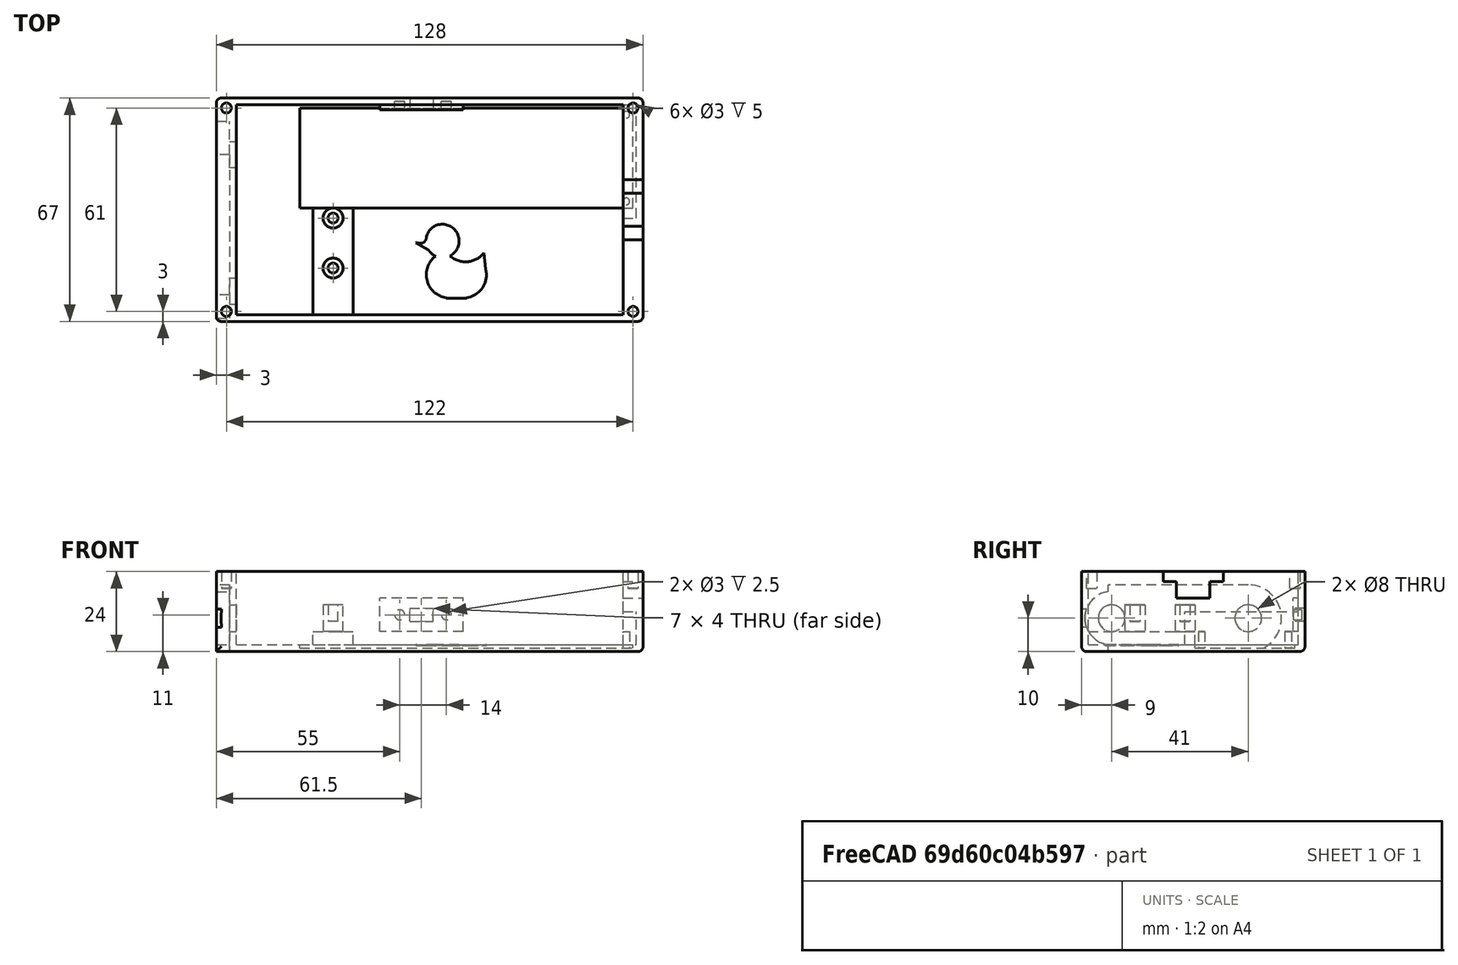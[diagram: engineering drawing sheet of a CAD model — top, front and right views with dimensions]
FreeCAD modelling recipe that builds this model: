
FCSTD DOCUMENT  (FreeCAD 1.0R39319 (Git))
Label: caseBottomV2
License: All rights reserved
LicenseURL: https://en.wikipedia.org/wiki/All_rights_reserved
objects: PartDesign::SubtractiveCylinder×16, PartDesign::SubtractiveBox×9, PartDesign::AdditiveCylinder×6, PartDesign::AdditiveBox×3, PartDesign::Fillet×1, PartDesign::SubtractivePrism×1, PartDesign::Body×1
note: 109 computed .brp shape members not serialized (recipe doc carries the construction recipe); baked Part::Feature solids carry a one-line shape summary decoded from their .brp

FEATURE [PartDesign::AdditiveBox] Box  label="base"
  AttacherType = Attacher::AttachEngine3D
  Height = 24
  Length = 128
  Refine = true
  Suppressed = false
  Width = 67
FEATURE [PartDesign::SubtractiveBox] Box001  label="primaryHollow"
  AttacherType = Attacher::AttachEngine3D
  AttachmentOffset = pos=(6,2,-22) rot=(0,0,1;0rad)
  AttachmentSupport = -> [Box]
  BaseFeature = -> Box
  Height = 22
  Length = 116
  MapMode = 5
  Placement = pos=(6,2,2) rot=(0,0,1;0rad)
  Refine = true
  Suppressed = false
  Width = 63
FEATURE [PartDesign::SubtractiveBox] Box002  label="batteryPCBRearNotch"
  AttacherType = Attacher::AttachEngine3D
  AttachmentOffset = pos=(116,29,0) rot=(0,0,1;0rad)
  AttachmentSupport = -> [Box001]
  BaseFeature = -> Box001
  Height = 10
  Length = 4
  MapMode = 5
  Placement = pos=(122,31,2) rot=(0,0,1;0rad)
  Refine = true
  Suppressed = false
  Width = 34
FEATURE [PartDesign::SubtractiveBox] Box003  label="batteryPCBRecess"
  AttacherType = Attacher::AttachEngine3D
  AttachmentOffset = pos=(-97,3,-1) rot=(0,0,1;0rad)
  AttachmentSupport = -> [Box002]
  BaseFeature = -> Box002
  Height = 1
  Length = 100
  MapMode = 5
  Placement = pos=(25,34,1) rot=(0,0,1;0rad)
  Refine = true
  Suppressed = false
  Width = 30
FEATURE [PartDesign::AdditiveBox] Box004  label="DACRearStand"
  AttacherType = Attacher::AttachEngine3D
  AttachmentOffset = pos=(4,-32,1) rot=(0,0,1;0rad)
  AttachmentSupport = -> [Box003]
  BaseFeature = -> Box003
  Height = 4
  Length = 12
  MapMode = 2
  Placement = pos=(29,2,2) rot=(0,0,1;0rad)
  Refine = true
  Suppressed = false
  Width = 32
FEATURE [PartDesign::AdditiveCylinder] Cylinder  label="DACLeftScrewSupport"
  Angle = 360
  AttacherType = Attacher::AttachEngine3D
  AttachmentOffset = pos=(6,14,0) rot=(0,0,1;0rad)
  AttachmentSupport = -> [Box004]
  BaseFeature = -> Box004
  FirstAngle = 0
  Height = 8
  MapMode = 5
  Placement = pos=(35,16,6) rot=(0,0,1;0rad)
  Radius = 3
  Refine = true
  SecondAngle = 0
  Suppressed = false
FEATURE [PartDesign::AdditiveCylinder] Cylinder001  label="DACRightScrewSupport"
  Angle = 360
  AttacherType = Attacher::AttachEngine3D
  AttachmentOffset = pos=(0,15,0) rot=(0,0,1;0rad)
  AttachmentSupport = -> [Cylinder]
  BaseFeature = -> Cylinder
  FirstAngle = 0
  Height = 8
  MapMode = 5
  Placement = pos=(35,31,6) rot=(0,0,1;0rad)
  Radius = 3
  Refine = true
  SecondAngle = 0
  Suppressed = false
FEATURE [PartDesign::SubtractiveCylinder] Cylinder002  label="DACRightScrewHollow"
  Angle = 360
  AttacherType = Attacher::AttachEngine3D
  AttachmentOffset = pos=(0,0,-5) rot=(0,0,1;0rad)
  AttachmentSupport = -> [Cylinder001]
  BaseFeature = -> Cylinder001
  FirstAngle = 0
  Height = 5
  MapMode = 5
  Placement = pos=(35,31,9) rot=(0,0,1;0rad)
  Radius = 1.5
  Refine = true
  SecondAngle = 0
  Suppressed = false
FEATURE [PartDesign::SubtractiveCylinder] Cylinder003  label="DACLeftScrewHollow"
  Angle = 360
  AttacherType = Attacher::AttachEngine3D
  AttachmentOffset = pos=(0,-15,-5) rot=(0,0,1;0rad)
  AttachmentSupport = -> [Cylinder002]
  BaseFeature = -> Cylinder002
  FirstAngle = 0
  Height = 5
  MapMode = 5
  Placement = pos=(35,16,9) rot=(0,0,1;0rad)
  Radius = 1.5
  Refine = true
  SecondAngle = 0
  Suppressed = false
FEATURE [PartDesign::SubtractiveBox] Box005  label="DACInset"
  AttacherType = Attacher::AttachEngine3D
  AttachmentOffset = pos=(-34,-9,-4) rot=(0,0,1;0rad)
  AttachmentSupport = -> [Cylinder003]
  BaseFeature = -> Cylinder003
  Height = 4
  Length = 42
  MapMode = 5
  Placement = pos=(4,50,0) rot=(0.57735,-0.57735,-0.57735;2.0944rad)
  Refine = true
  Suppressed = false
  Width = 20
FEATURE [PartDesign::SubtractiveCylinder] Cylinder004  label="volumeKnobHole"
  Angle = 360
  AttacherType = Attacher::AttachEngine3D
  AttachmentOffset = pos=(0,10,-6) rot=(0,0,1;0rad)
  AttachmentSupport = -> [Box005]
  BaseFeature = -> Box005
  FirstAngle = 0
  Height = 6
  MapMode = 5
  Placement = pos=(6,50,10) rot=(0.57735,-0.57735,-0.57735;2.0944rad)
  Radius = 4
  Refine = true
  SecondAngle = 0
  Suppressed = false
FEATURE [PartDesign::SubtractiveCylinder] Cylinder005  label="headphoneJackHole"
  Angle = 360
  AttacherType = Attacher::AttachEngine3D
  AttachmentOffset = pos=(41,0,-6) rot=(0,0,1;0rad)
  AttachmentSupport = -> [Cylinder004]
  BaseFeature = -> Cylinder004
  FirstAngle = 0
  Height = 6
  MapMode = 5
  Placement = pos=(6,9,10) rot=(0.57735,-0.57735,-0.57735;2.0944rad)
  Radius = 4
  Refine = true
  SecondAngle = 0
  Suppressed = false
FEATURE [PartDesign::SubtractiveCylinder] Cylinder006  label="volumeKnobRecess"
  Angle = 360
  AttacherType = Attacher::AttachEngine3D
  AttachmentOffset = pos=(-41,0,-4) rot=(0,0,1;0rad)
  AttachmentSupport = -> [Cylinder005]
  BaseFeature = -> Cylinder005
  FirstAngle = 0
  Height = 4
  MapMode = 5
  Placement = pos=(4,50,10) rot=(0.57735,-0.57735,-0.57735;2.0944rad)
  Radius = 10
  Refine = true
  SecondAngle = 0
  Suppressed = false
FEATURE [PartDesign::SubtractiveCylinder] Cylinder007  label="headphoneJackRecess"
  Angle = 360
  AttacherType = Attacher::AttachEngine3D
  AttachmentOffset = pos=(41,0,-4) rot=(0,0,1;0rad)
  AttachmentSupport = -> [Cylinder006]
  BaseFeature = -> Cylinder006
  FirstAngle = 0
  Height = 4
  MapMode = 5
  Placement = pos=(4,9,10) rot=(0.57735,-0.57735,-0.57735;2.0944rad)
  Radius = 8
  Refine = true
  SecondAngle = 0
  Suppressed = false
FEATURE [PartDesign::AdditiveBox] Box006  label="powerSwitchBase"
  AttacherType = Attacher::AttachEngine3D
  AttachmentOffset = pos=(-4,-70,0) rot=(0,0,1;0rad)
  AttachmentSupport = -> [Cylinder007]
  BaseFeature = -> Cylinder007
  Height = 1.5
  Length = 10
  MapMode = 5
  Placement = pos=(74,65,6) rot=(0.57735,-0.57735,0.57735;2.0944rad)
  Refine = true
  Suppressed = false
  Width = 25
FEATURE [PartDesign::SubtractiveBox] Box007  label="powerSwitchCutout"
  AttacherType = Attacher::AttachEngine3D
  AttachmentOffset = pos=(3,9,-4) rot=(0,0,1;0rad)
  AttachmentSupport = -> [Box006]
  BaseFeature = -> Box006
  Height = 6
  Length = 4
  MapMode = 5
  Placement = pos=(65,67.5,9) rot=(0.57735,-0.57735,0.57735;2.0944rad)
  Refine = true
  Suppressed = false
  Width = 7
FEATURE [PartDesign::SubtractiveCylinder] Cylinder008  label="powerSwitchHollowBottom"
  Angle = 360
  AttacherType = Attacher::AttachEngine3D
  AttachmentOffset = pos=(2,-4,-2.5) rot=(0,0,1;0rad)
  AttachmentSupport = -> [Box007]
  BaseFeature = -> Box007
  FirstAngle = 0
  Height = 2.5
  MapMode = 5
  Placement = pos=(69,66,11) rot=(0.57735,-0.57735,0.57735;2.0944rad)
  Radius = 1.5
  Refine = true
  SecondAngle = 0
  Suppressed = false
FEATURE [PartDesign::SubtractiveCylinder] Cylinder009  label="powerSwitchHollowTop"
  Angle = 360
  AttacherType = Attacher::AttachEngine3D
  AttachmentOffset = pos=(0,14,-2.5) rot=(0,0,1;0rad)
  AttachmentSupport = -> [Cylinder008]
  BaseFeature = -> Cylinder008
  FirstAngle = 0
  Height = 2.5
  MapMode = 5
  Placement = pos=(55,66,11) rot=(0.57735,-0.57735,0.57735;2.0944rad)
  Radius = 1.5
  Refine = true
  SecondAngle = 0
  Suppressed = false
FEATURE [PartDesign::AdditiveCylinder] Cylinder010  label="batteryPCBSupportLeft"
  Angle = 360
  AttacherType = Attacher::AttachEngine3D
  AttachmentOffset = pos=(-68,30,0) rot=(0,0,1;0rad)
  AttachmentSupport = -> [Cylinder009]
  BaseFeature = -> Cylinder009
  FirstAngle = 0
  Height = 5
  MapMode = 5
  Placement = pos=(123,36,1) rot=(0,0,1;3.14159rad)
  Radius = 1
  Refine = true
  SecondAngle = 0
  Suppressed = false
FEATURE [PartDesign::AdditiveCylinder] Cylinder011  label="batteryPCBSupportRight"
  Angle = 360
  AttacherType = Attacher::AttachEngine3D
  AttachmentOffset = pos=(0,-26,0) rot=(0,0,1;0rad)
  AttachmentSupport = -> [Cylinder010]
  BaseFeature = -> Cylinder010
  FirstAngle = 0
  Height = 5
  MapMode = 5
  Placement = pos=(123,62,1) rot=(0,0,1;3.14159rad)
  Radius = 1
  Refine = true
  SecondAngle = 0
  Suppressed = false
FEATURE [PartDesign::SubtractiveBox] Box008  label="chargePortCutout1"
  AttacherType = Attacher::AttachEngine3D
  AttachmentOffset = pos=(-37.5,20,-6) rot=(0,0,1;0rad)
  AttachmentSupport = -> [Cylinder011]
  BaseFeature = -> Cylinder011
  Height = 6
  Length = 18
  MapMode = 5
  Placement = pos=(122,24.5,21) rot=(0.57735,0.57735,0.57735;2.0944rad)
  Refine = true
  Suppressed = false
  Width = 3
FEATURE [PartDesign::SubtractiveBox] Box009  label="chargePortCutout2"
  AttacherType = Attacher::AttachEngine3D
  AttachmentOffset = pos=(4,-5,-6) rot=(0,0,1;0rad)
  AttachmentSupport = -> [Box008]
  BaseFeature = -> Box008
  Height = 6
  Length = 10
  MapMode = 5
  Placement = pos=(122,28.5,16) rot=(0.57735,0.57735,0.57735;2.0944rad)
  Refine = true
  Suppressed = false
  Width = 5
FEATURE [PartDesign::SubtractiveCylinder] Cylinder012  label="topLeftScrew"
  Angle = 360
  AttacherType = Attacher::AttachEngine3D
  AttachmentOffset = pos=(25.5,-119,-5) rot=(0,0,1;0rad)
  AttachmentSupport = -> [Box009]
  BaseFeature = -> Box009
  FirstAngle = 0
  Height = 5
  MapMode = 5
  Placement = pos=(3,3,19) rot=(0,0,-1;1.5708rad)
  Radius = 1.5
  Refine = true
  SecondAngle = 0
  Suppressed = false
FEATURE [PartDesign::SubtractiveCylinder] Cylinder013  label="topRightScrew"
  Angle = 360
  AttacherType = Attacher::AttachEngine3D
  AttachmentOffset = pos=(-61,0,-5) rot=(0,0,1;0rad)
  AttachmentSupport = -> [Cylinder012]
  BaseFeature = -> Cylinder012
  FirstAngle = 0
  Height = 5
  MapMode = 5
  Placement = pos=(3,64,19) rot=(0,0,-1;1.5708rad)
  Radius = 1.5
  Refine = true
  SecondAngle = 0
  Suppressed = false
FEATURE [PartDesign::SubtractiveCylinder] Cylinder014  label="bottomRightScrew"
  Angle = 360
  AttacherType = Attacher::AttachEngine3D
  AttachmentOffset = pos=(0,122,-5) rot=(0,0,1;0rad)
  AttachmentSupport = -> [Cylinder013]
  BaseFeature = -> Cylinder013
  FirstAngle = 0
  Height = 5
  MapMode = 5
  Placement = pos=(125,64,19) rot=(0,0,-1;1.5708rad)
  Radius = 1.5
  Refine = true
  SecondAngle = 0
  Suppressed = false
FEATURE [PartDesign::SubtractiveCylinder] Cylinder015  label="bottomLeftScrew"
  Angle = 360
  AttacherType = Attacher::AttachEngine3D
  AttachmentOffset = pos=(61,0,-5) rot=(0,0,1;0rad)
  AttachmentSupport = -> [Cylinder014]
  BaseFeature = -> Cylinder014
  FirstAngle = 0
  Height = 5
  MapMode = 5
  Placement = pos=(125,3,19) rot=(0,0,-1;1.5708rad)
  Radius = 1.5
  Refine = true
  SecondAngle = 0
  Suppressed = false
FEATURE [PartDesign::Fillet] Fillet
  Base = -> Cylinder015 [Edge34,Edge22,Edge13,Edge12,Edge23,Edge1,Edge10]
  BaseFeature = -> Cylinder015
  Placement = pos=(125,3,19) rot=(0,0,-1;1.5708rad)
  Radius = 1.5
  Refine = true
  SupportTransform = false
  Suppressed = false
  UseAllEdges = false
FEATURE [PartDesign::SubtractiveCylinder] Cylinder016
  Angle = 360
  AttacherType = Attacher::AttachEngine3D
  AttachmentOffset = pos=(-21,-57,-0.2) rot=(0,0,1;0rad)
  AttachmentSupport = -> [Fillet]
  BaseFeature = -> Fillet
  FirstAngle = 0
  Height = 0.2
  MapMode = 5
  Placement = pos=(68,24,1.8) rot=(0,0,-1;1.5708rad)
  Radius = 5
  Refine = true
  SecondAngle = 0
  Suppressed = false
FEATURE [PartDesign::SubtractiveCylinder] Cylinder017
  Angle = 360
  AttacherType = Attacher::AttachEngine3D
  AttachmentOffset = pos=(10,2,-0.2) rot=(0,0,1;0rad)
  AttachmentSupport = -> [Cylinder016]
  BaseFeature = -> Cylinder016
  FirstAngle = 0
  Height = 0.2
  MapMode = 5
  Placement = pos=(70,14,1.8) rot=(0,0,-1;1.5708rad)
  Radius = 7
  Refine = true
  SecondAngle = 0
  Suppressed = false
FEATURE [PartDesign::SubtractiveCylinder] Cylinder018
  Angle = 360
  AttacherType = Attacher::AttachEngine3D
  AttachmentOffset = pos=(0,4,-0.2) rot=(0,0,1;0rad)
  AttachmentSupport = -> [Cylinder017]
  BaseFeature = -> Cylinder017
  FirstAngle = 0
  Height = 0.2
  MapMode = 5
  Placement = pos=(74,14,1.8) rot=(0,0,-1;1.5708rad)
  Radius = 7
  Refine = true
  SecondAngle = 0
  Suppressed = false
FEATURE [PartDesign::SubtractiveBox] Box010
  AttacherType = Attacher::AttachEngine3D
  AttachmentOffset = pos=(2,-5,-0.2) rot=(0,0,1;0rad)
  AttachmentSupport = -> [Cylinder018]
  BaseFeature = -> Cylinder018
  Height = 0.2
  Length = 5
  MapMode = 5
  Placement = pos=(69,12,1.8) rot=(0,0,-1;1.5708rad)
  Refine = true
  Suppressed = false
  Width = 6
FEATURE [PartDesign::SubtractiveBox] Box011
  AttacherType = Attacher::AttachEngine3D
  AttachmentOffset = pos=(-10,7.1,-0.2) rot=(0,0,1;0.10472rad)
  AttachmentSupport = -> [Box010]
  BaseFeature = -> Box010
  Height = 0.2
  Length = 9
  MapMode = 5
  Placement = pos=(76.1,22,1.8) rot=(0,0,-1;1.46608rad)
  Refine = true
  Suppressed = false
  Width = 4
FEATURE [PartDesign::AdditiveCylinder] Cylinder019
  Angle = 360
  AttacherType = Attacher::AttachEngine3D
  AttachmentOffset = pos=(-3,-1,-0.2) rot=(0,0,1;0rad)
  AttachmentSupport = -> [Box011]
  BaseFeature = -> Box011
  FirstAngle = 0
  Height = 0.2
  MapMode = 5
  Placement = pos=(74.7919,24.879,1.8) rot=(0,0,-1;1.46608rad)
  Radius = 7
  Refine = true
  SecondAngle = 0
  Suppressed = false
FEATURE [PartDesign::SubtractiveCylinder] Cylinder020
  Angle = 360
  AttacherType = Attacher::AttachEngine3D
  AttachmentOffset = pos=(0,-7,-0.2) rot=(0,0,1;0rad)
  AttachmentSupport = -> [Cylinder019]
  BaseFeature = -> Cylinder019
  FirstAngle = 0
  Height = 0.2
  MapMode = 5
  Placement = pos=(67.8302,24.1473,1.8) rot=(0,0,-1;1.46608rad)
  Radius = 5
  Refine = true
  SecondAngle = 0
  Suppressed = false
FEATURE [PartDesign::SubtractivePrism] Prism
  AttacherType = Attacher::AttachEngine3D
  AttachmentOffset = pos=(0,-5.5,-0.2) rot=(0,0,1;0.418879rad)
  AttachmentSupport = -> [Cylinder020]
  BaseFeature = -> Cylinder020
  Circumradius = 2.5
  FirstAngle = 0
  Height = 0.2
  MapMode = 5
  Placement = pos=(62.3604,23.5724,1.8) rot=(0,0,-1;1.0472rad)
  Polygon = 3
  Refine = true
  SecondAngle = 0
  Suppressed = false
FEATURE [PartDesign::AdditiveCylinder] Cylinder021
  Angle = 360
  AttacherType = Attacher::AttachEngine3D
  AttachmentOffset = pos=(-2,-0.2,-0.2) rot=(0,0,1;0rad)
  AttachmentSupport = -> [Box001]
  BaseFeature = -> Prism
  FirstAngle = 0
  Height = 0.2
  MapMode = 5
  Placement = pos=(61.1872,25.2045,1.8) rot=(0,0,-1;1.0472rad)
  Radius = 1.8
  Refine = true
  SecondAngle = 0
  Suppressed = false
FEATURE [PartDesign::Body] Body
  AllowCompound = false
  Group = -> [Box,Box001,Box002,Box003,Box004,Cylinder,Cylinder001,Cylinder002,Cylinder003,Box005,Cylinder004,Cylinder005,Cylinder006,Cylinder007,Box006,Box007,Cylinder008,Cylinder009,Cylinder010,Cylinder011,Box008,Box009,Cylinder012,Cylinder013,Cylinder014,Cylinder015,Fillet,Cylinder016,Cylinder017,Cylinder018,Box010,Box011,Cylinder019,Cylinder020,Prism,Cylinder021]
  Origin = -> Origin
  Tip = -> Cylinder021
